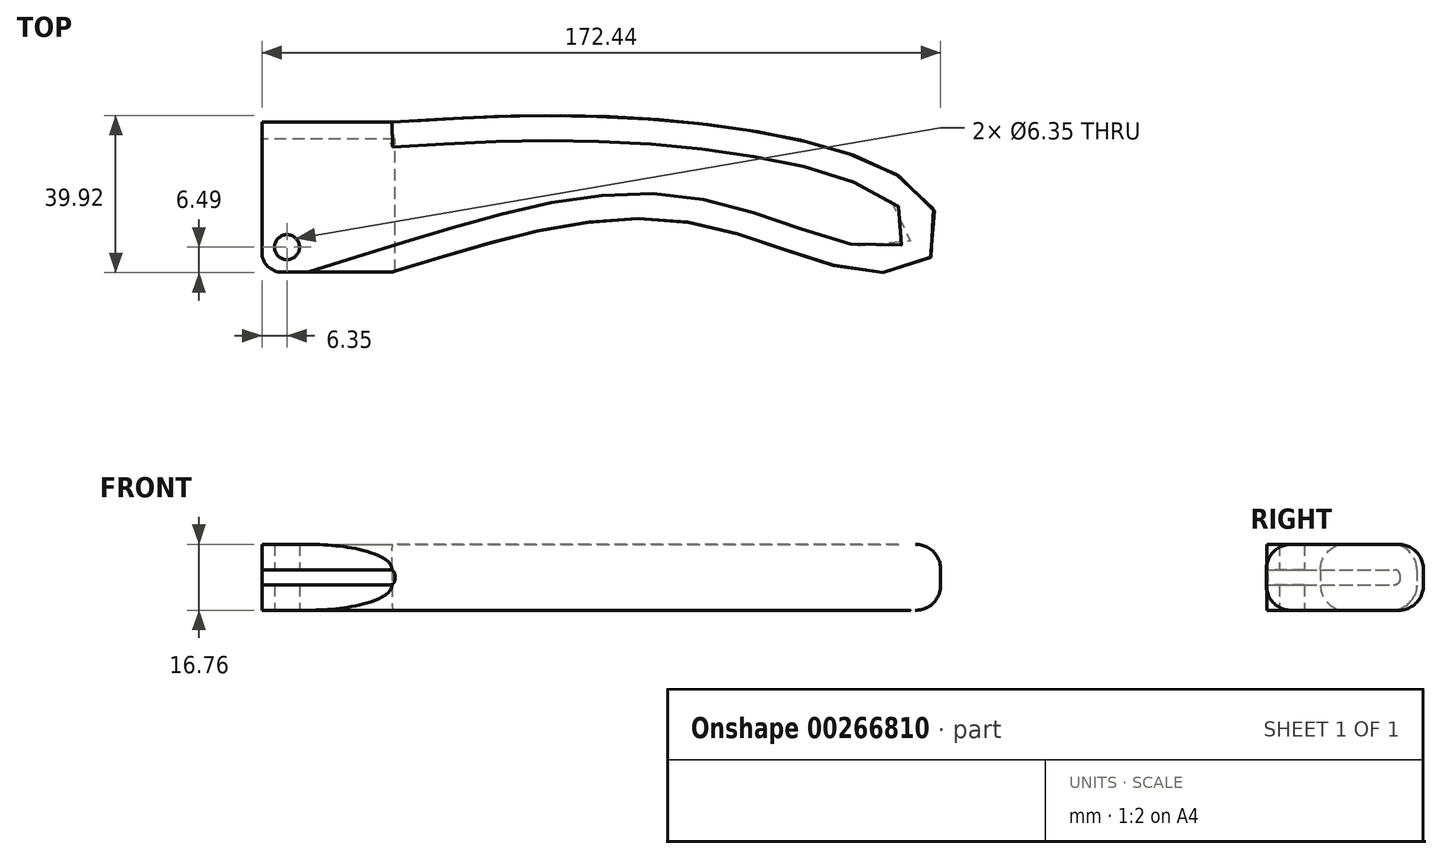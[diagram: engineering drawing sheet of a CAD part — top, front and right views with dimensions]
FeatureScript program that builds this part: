
annotation { "Feature Type Name" : "Feature", "Feature Type Description" : "" }
export const myFeature = defineFeature(function(context is Context, id is Id, definition is map)
    precondition{}
    {
        {
            var Q0;
            Q0=qCreatedBy(makeId("Top.planeOp"),FACE);
            var sketch = newSketch(context, id + "F0", { "sketchPlane" : qUnion([Q0])});
            skLineSegment(sketch, "E0.bottom", {"start": v(0, 0) * mm, "end": v(33.02, 0) * mm});
            skLineSegment(sketch, "E0.top", {"start": v(0, 38.1) * mm, "end": v(33.02, 38.1) * mm});
            skLineSegment(sketch, "E0.left", {"start": v(0, 0) * mm, "end": v(0, 38.1) * mm});
            skLineSegment(sketch, "E0.right", {"start": v(33.02, 0) * mm, "end": v(33.02, 38.1) * mm});
            skFitSpline(sketch, "E1", {"points": [v(33.02, 0) * mm, v(105.77, 13.06) * mm, v(154.03, 0) * mm, v(171.63, 6.17) * mm, v(165.1, 22.13) * mm, v(97.06, 39) * mm, v(33.02, 38.1) * mm], "startDerivative": vector(359.44, 112) * mm, "endDerivative": vector(-305.99, -19.27) * mm});
            skCircle(sketch, "E2", {"center": v(6.35, 6.35) * mm, "radius": 3.18 * mm});
            skSolve(sketch);
        }
        {
            var Q0;
            Q0=makeQuery(id+"F0.imprint","IMPRINT",FACE,{"disambiguationData":[TD([[makeQuery(id+"F0.imprint","IMPRINT",EDGE,{"derivedFrom":sQuery(id+"F0.wireOp",EDGE,"E0.right")}),-1.0]])]});
            var Q1;
            Q1=makeQuery(id+"F0.imprint","IMPRINT",FACE,{"disambiguationData":[TD([[makeQuery(id+"F0.imprint","IMPRINT",EDGE,{"derivedFrom":sQuery(id+"F0.wireOp",EDGE,"E0.bottom")}),1.0]])]});
            extrude(context, id + "F1", {"entities" : qUnion([Q0, Q1]), "depth" : 16.76 * mm});
        }
        {
            var Q0;
            Q0=makeQuery(id+"F1.opExtrude","CAP_EDGE",EDGE,{"disambiguationData":[OSD([sQuery(id+"F0.wireOp",EDGE,"E1")])],"isStart":false});
            var Q1;
            Q1=makeQuery(id+"F1.opExtrude","CAP_EDGE",EDGE,{"disambiguationData":[OSD([sQuery(id+"F0.wireOp",EDGE,"E1")])],"isStart":true});
            fillet(context, id + "F2", {"entities" : qUnion([Q0, Q1]), "radius" : 6.35 * mm, "tangentPropagation" : true, "allowEdgeOverflow" : false});
        }
        {
            var Q0;
            Q0=makeQuery(id+"F1.opExtrude","SWEPT_FACE",FACE,{"disambiguationData":[OSD([sQuery(id+"F0.wireOp",EDGE,"E0.left")])]});
            var sketch = newSketch(context, id + "F3", { "sketchPlane" : qUnion([Q0])});
            skLineSegment(sketch, "E3.bottom", {"start": v(0, 10.29) * mm, "end": v(-33.78, 10.29) * mm});
            skLineSegment(sketch, "E3.top", {"start": v(0, 6.48) * mm, "end": v(-33.78, 6.48) * mm});
            skLineSegment(sketch, "E3.left", {"start": v(0, 10.29) * mm, "end": v(0, 6.48) * mm});
            skLineSegment(sketch, "E3.right", {"start": v(-33.78, 10.29) * mm, "end": v(-33.78, 6.48) * mm});
            skLineSegment(sketch, "E4", {"start": v(-16.9, 10.29) * mm, "end": v(-16.9, 16.76) * mm, "construction": true});
            skLineSegment(sketch, "E5", {"start": v(-16.9, 6.48) * mm, "end": v(-16.9, 0) * mm, "construction": true});
            skSolve(sketch);
        }
        {
            var Q0;
            Q0=makeQuery(id+"F3.imprint","IMPRINT",FACE,{"disambiguationData":[TD([[makeQuery(id+"F3.imprint","IMPRINT",EDGE,{"derivedFrom":sQuery(id+"F3.wireOp",EDGE,"E3.bottom")}),1.0]])]});
            extrude(context, id + "F4", {"entities" : qUnion([Q0]), "operationType" : NewBodyOperationType.REMOVE, "oppositeDirection" : true, "depth" : 33.78 * mm});
        }
        {
            var Q0;
            {var subQ0=sQuery(id+"F0.wireOp",EDGE,"E0.bottom");var subQ1=sQuery(id+"F0.wireOp",EDGE,"E0.left");Q0=makeQuery(id+"F4.boolean.opBoolean","SPLIT",EDGE,{"disambiguationData":[TD([makeQuery(id+"F4.opExtrude","SWEPT_FACE",FACE,{"disambiguationData":[OSD([sQuery(id+"F3.wireOp",EDGE,"E3.bottom")])]})])],"derivedFrom":makeQuery(id+"F1.opExtrude","SWEPT_EDGE",EDGE,{"disambiguationData":[OSD([subQ0,subQ1])]})});}
            var Q1;
            {var subQ0=sQuery(id+"F0.wireOp",EDGE,"E0.bottom");var subQ1=sQuery(id+"F0.wireOp",EDGE,"E0.left");Q1=makeQuery(id+"F4.boolean.opBoolean","SPLIT",EDGE,{"disambiguationData":[TD([makeQuery(id+"F4.opExtrude","SWEPT_FACE",FACE,{"disambiguationData":[OSD([sQuery(id+"F3.wireOp",EDGE,"E3.top")])]})])],"derivedFrom":makeQuery(id+"F1.opExtrude","SWEPT_EDGE",EDGE,{"disambiguationData":[OSD([subQ0,subQ1])]})});}
            fillet(context, id + "F5", {"entities" : qUnion([Q0, Q1]), "radius" : 5.08 * mm, "tangentPropagation" : true, "allowEdgeOverflow" : false});
        }
        {
            var Q0;
            Q0=makeQuery(id+"F4.boolean.opBoolean","COPY",EDGE,{"derivedFrom":makeQuery(id+"F4.opExtrude","CAP_EDGE",EDGE,{"disambiguationData":[OSD([sQuery(id+"F3.wireOp",EDGE,"E3.top")])],"isStart":false})});
            var Q1;
            Q1=makeQuery(id+"F4.boolean.opBoolean","COPY",EDGE,{"derivedFrom":makeQuery(id+"F4.opExtrude","CAP_EDGE",EDGE,{"disambiguationData":[OSD([sQuery(id+"F3.wireOp",EDGE,"E3.bottom")])],"isStart":false})});
            var Q2;
            Q2=makeQuery(id+"F4.boolean.opBoolean","COPY",EDGE,{"derivedFrom":makeQuery(id+"F4.opExtrude","SWEPT_EDGE",EDGE,{"disambiguationData":[OSD([sQuery(id+"F3.wireOp",EDGE,"E3.top"),sQuery(id+"F3.wireOp",EDGE,"E3.right")])]})});
            var Q3;
            Q3=makeQuery(id+"F4.boolean.opBoolean","COPY",EDGE,{"derivedFrom":makeQuery(id+"F4.opExtrude","SWEPT_EDGE",EDGE,{"disambiguationData":[OSD([sQuery(id+"F3.wireOp",EDGE,"E3.bottom"),sQuery(id+"F3.wireOp",EDGE,"E3.right")])]})});
            fillet(context, id + "F6", {"entities" : qUnion([Q0, Q1, Q2, Q3]), "radius" : 1.27 * mm, "tangentPropagation" : true, "allowEdgeOverflow" : false});
        }
    });
